# Revit family: Furniture_Tables_Svedholm_Offset
name_source: partatom
category: Furniture
revit_build: Autodesk Revit 2018 (Build: 20190510_1515(x64)
units: mm (PartAtom-declared; Revit-internal decimal feet)

## family parameters
Always vertical = No
Cut with Voids When Loaded = No
OmniClass Number = 23.21.23.00
OmniClass Title = Residential Furniture and Equipment
Room Calculation Point = No
Shared = No
Work Plane-Based = Yes

## types (4) — shared parameters
BIMobject category = Tables
Default Elevation = 1219 mm
Description = A side table with table top of Dekton alternatively tempered glass with ceramic paint. Table base of powder coated wire.
Design country = Sweden
Edition number = 1
IFC Classification = Furniture
Manufacturer = Svedholm
Manufacturer country = Sweden
Manufacturer name = Svedholm
Material main = Mineral Marble
Material secondary = Powder coated steel
Model = Offset
OmniClass Code = 23-21 23 00
OmniClass Description = Residential Furniture and Equipment
Product Guid = 4830ee14-1da5-4138-b0a7-98194682c401
Product SKU = Offset
Product data url = https://bimobject.com
Product family = Offset
Product group = Tables
Product name = Offset
Product url = https://www.svedholm.se
QR code = https://bimobject.com
Secondary material = Svedholm - Glass - Transparent
UNSPSC Code = 56
URL = https://www.svedholm.se
Uniclass 1.4 Code = L8221
Uniclass 1.4 Description = Tables

## per-type parameters (varying)
| type | 400x400 Dekton | 400x400mm | 400x400mm Glass | 400x800 Dekton | 400x800mm | 400x800mm Glass |
| ART - (207.600.001) Tabletop material - (Dekton) Tabletop dim. - (400x400) | Yes | Yes | No | No | No | No |
| ART - (207.600.003) Tabletop material - (Glass) Tabletop dim. - (400x400) | No | Yes | Yes | No | No | No |
| ART - (207.600.002) Tabletop material - (Dekton) Tabletop dim. - (400x800) | No | No | No | Yes | Yes | No |
| ART - (207.600.004) Tabletop material - (Glass) Tabletop dim. - (400x800) | No | No | No | No | Yes | Yes |

## geometry (parser evidence)
native form markers: Sweep x2
no freeform markers — native parametric forms only
